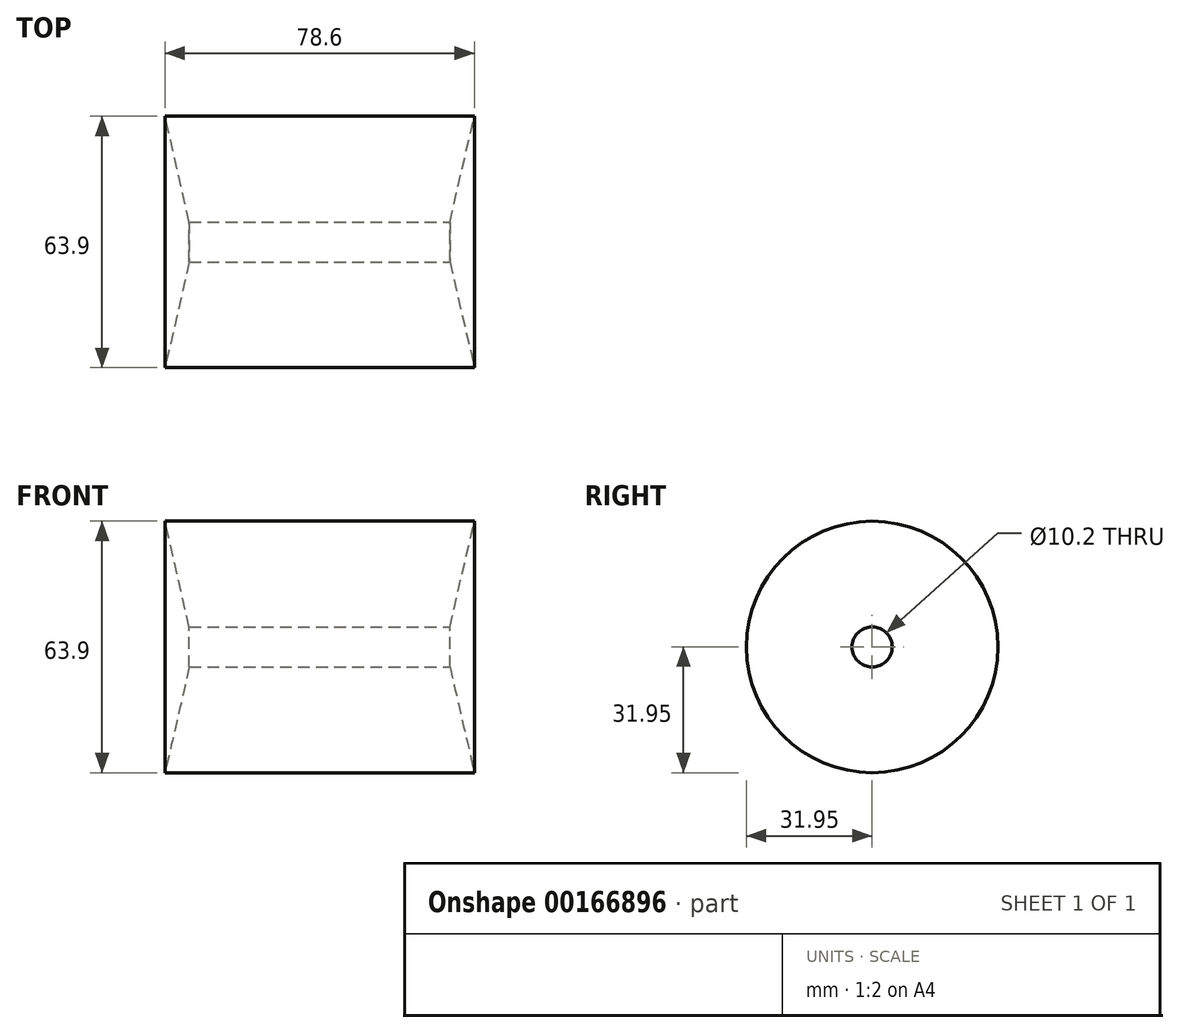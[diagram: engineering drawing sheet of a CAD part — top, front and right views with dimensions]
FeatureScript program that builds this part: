
annotation { "Feature Type Name" : "Feature", "Feature Type Description" : "" }
export const myFeature = defineFeature(function(context is Context, id is Id, definition is map)
    precondition{}
    {
        {
            var Q0;
            Q0=qCreatedBy(makeId("Front.planeOp"),FACE);
            var sketch = newSketch(context, id + "F0", { "sketchPlane" : qUnion([Q0])});
            skLineSegment(sketch, "E0", {"start": v(0, 5.1) * mm, "end": v(-66.2, 5.1) * mm});
            skLineSegment(sketch, "E1", {"start": v(0, 5.1) * mm, "end": v(6.2, 31.95) * mm});
            skLineSegment(sketch, "E2", {"start": v(0, 0) * mm, "end": v(-58.77, 0) * mm, "construction": true});
            skLineSegment(sketch, "E3", {"start": v(6.2, 31.95) * mm, "end": v(-72.4, 31.95) * mm});
            skLineSegment(sketch, "E4", {"start": v(6.2, 31.95) * mm, "end": v(9.4, 31.95) * mm, "construction": true});
            skLineSegment(sketch, "E5", {"start": v(-66.2, 5.1) * mm, "end": v(-72.4, 31.95) * mm});
            skLineSegment(sketch, "E6", {"start": v(-72.4, 31.95) * mm, "end": v(-75.6, 31.95) * mm, "construction": true});
            skSolve(sketch);
        }
        {
            var Q0;
            Q0 = qSketchRegion(id + "F0", true);
            var Q1;
            Q1=sQuery(id+"F0.wireOp",EDGE,"E2");
            revolve(context, id + "F1", {"entities" : qUnion([Q0]), "axis" : qUnion([Q1]), "revolveType" : RevolveType.FULL});
        }
    });
